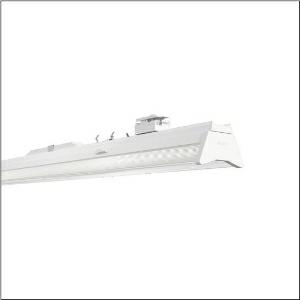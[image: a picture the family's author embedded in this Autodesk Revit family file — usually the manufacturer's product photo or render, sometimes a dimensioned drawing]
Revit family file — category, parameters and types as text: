
# Revit family: licross_r__11_performance_mo_51tm16dn35xg_3127
name_source: partatom
category: Lighting Fixtures
units: mm (PartAtom-declared; Revit-internal decimal feet)

## family parameters
Cut with Voids When Loaded = No
Host = Face
Light Source = No
Part Type = Normal
Room Calculation Point = No
Round Connector Dimension = Use Diameter
Shared = No

## types (1)
- --- (1 x LED, 5100 lm, 28.3 W, 3000K)
    Apparent Load = 28 VA
    CIE Flux Codes = 66 88 96 79 100
    Color Rendering = 80
    Color Temperature = 3000K
    Default Elevation = 1800 mm
    Description = Licross® 11 Performance MO, luminaire insert, of sheet steel, galvanised, coil coated, white, length: 1.500mm, width: 120mm, height: 123mm, LED rated luminous flux: 5.100lm, light colour: 830, control gear: DALI 2, with plug, 5-pole, with phase selection, mains connection: 220..240V, AC, 50/60Hz, rated input power: 28.3W, internal wiring halogen-free, primary light control with lens, of plastic, primary optical cover: cover, of PMMA, light emission: direct/indirect distribution, primary light characteristic: symmetric, protection rating (complete): IP40, insulation class (complete): insulation class I (protective earthing), certification: CE, ENEC, VDE, UKCA, protection symbol: D if used in an environment without relevant dust loads with corresponding accessories, impact resistance: IK06, permissible ambient temperature for indoor applications: -25..+45°C, corresponds to IFS (International Featured Standards) requirements for safety and quality in the food industry, reducing of maximum allowable ambient temperature of 5°C with ceiling mounting, LABS conformity tested according to VDMA 24364:2018-05, packaging unit: 1 piece
    Height = 114 mm
    Lamp = 1 x LED
    Lamp Light Flux = 5100 lm
    Lamp Power = 28.3 W
    Lamp count = 1
    Length = 1500 mm
    Luminous efficacy = 180 lm/W
    Manufacturer = Siteco
    ModVariant = No
    Model = 51TM16DN35XG
    Mounting Place = Ceiling
    Mounting Type = Pendant
    Number of Poles = 1
    OnlyDefault = Yes
    Power Factor = 1
    Product Name = Licross® 11 Performance MO
    Product group = luminaire insert | ceiling pendant
    ProductGroupID = 902
    Protection Class = Protection class I
    Protection Degree = IP 40
    RLX_Detail_Level = 1
    RLX_Emergency_Light_Flux = 0 lm
    RLX_Emergency_Type = 0
    RLX_Emergency_Type_DB = No
    RlxData = <blob elided: 33829 chars, md5=0cb477a3>
    Socket = socket
    Standby Power = 0 W
    System Light Flux = 5100 lm
    System Power = 28 W
    Type Comments = factory setting: luminous flux: 100 % | dim-lin: 254 | 190 mA
    Type Image = l_1256138.jpg
    URL = http://relux.com
    VarID = @adj_089461
    Voltage = 0 V
    Weight = 0.00 kg
    Width = 120 mm

## geometry (parser evidence)
native form markers: Blend x4, Sweep x14
no freeform markers — native parametric forms only
